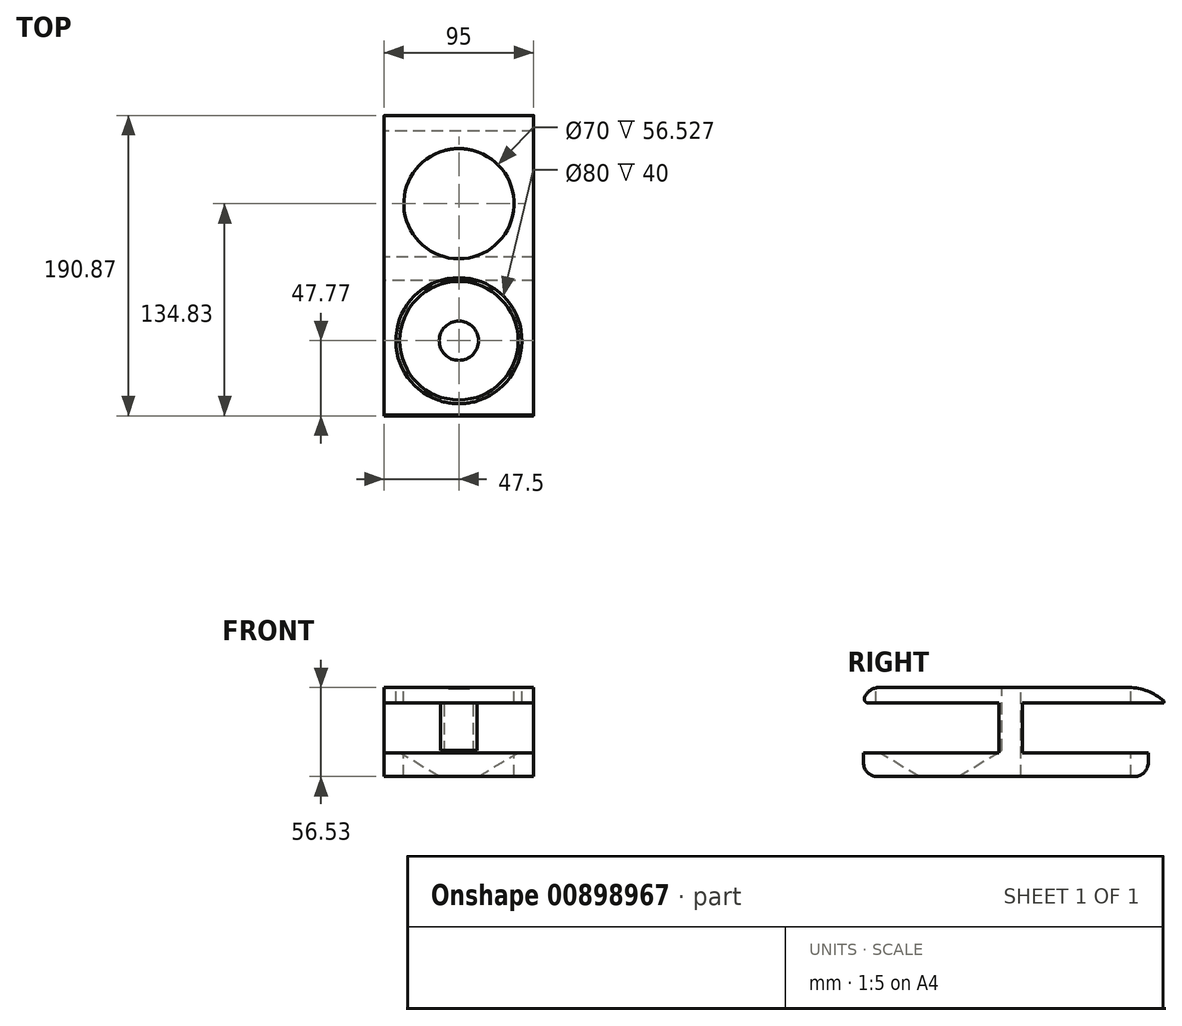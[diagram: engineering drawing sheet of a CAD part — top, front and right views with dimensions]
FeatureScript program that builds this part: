
annotation { "Feature Type Name" : "Feature", "Feature Type Description" : "" }
export const myFeature = defineFeature(function(context is Context, id is Id, definition is map)
    precondition{}
    {
        {
            var Q0;
            Q0=qCreatedBy(makeId("Right.planeOp"),FACE);
            var sketch = newSketch(context, id + "F0", { "sketchPlane" : qUnion([Q0])});
            skLineSegment(sketch, "E0", {"start": v(0, 11.66) * mm, "end": v(90.83, 11.66) * mm});
            skLineSegment(sketch, "E1", {"start": v(90.83, 11.66) * mm, "end": v(90.83, 1.76) * mm});
            skLineSegment(sketch, "E2", {"start": v(90.83, 1.76) * mm, "end": v(0, 1.76) * mm});
            skLineSegment(sketch, "E3", {"start": v(0, 1.76) * mm, "end": v(0, -29.77) * mm});
            skLineSegment(sketch, "E4", {"start": v(0, -29.77) * mm, "end": v(79.76, -29.77) * mm});
            skLineSegment(sketch, "E5", {"start": v(79.76, -29.77) * mm, "end": v(79.76, -44.87) * mm});
            skLineSegment(sketch, "E6", {"start": v(79.76, -44.87) * mm, "end": v(-101.06, -44.87) * mm});
            skLineSegment(sketch, "E7", {"start": v(-101.06, -44.87) * mm, "end": v(-101.06, -29.77) * mm});
            skLineSegment(sketch, "E8", {"start": v(-101.06, -29.77) * mm, "end": v(-15.01, -29.77) * mm});
            skLineSegment(sketch, "E9", {"start": v(-15.01, -29.77) * mm, "end": v(-15.01, 1.76) * mm});
            skLineSegment(sketch, "E10", {"start": v(-15.01, 1.76) * mm, "end": v(-101.06, 1.76) * mm});
            skLineSegment(sketch, "E11", {"start": v(-101.06, 1.76) * mm, "end": v(-101.06, 11.66) * mm});
            skLineSegment(sketch, "E12", {"start": v(-101.06, 11.66) * mm, "end": v(0, 11.66) * mm});
            skSolve(sketch);
        }
        {
            var Q0;
            Q0=makeQuery(id+"F0.imprint","IMPRINT",FACE,{"disambiguationData":[TD([[makeQuery(id+"F0.imprint","IMPRINT",EDGE,{"derivedFrom":sQuery(id+"F0.wireOp",EDGE,"E0")}),-1.0]])]});
            extrude(context, id + "F1", {"entities" : qUnion([Q0]), "depth" : 95 * mm, "offsetDistance" : 25 * mm});
        }
        {
            var Q0;
            Q0=makeQuery(id+"F1.opExtrude","SWEPT_EDGE",EDGE,{"disambiguationData":[OSD([sQuery(id+"F0.wireOp",EDGE,"E11"),sQuery(id+"F0.wireOp",EDGE,"E12")])]});
            fillet(context, id + "F2", {"entities" : qUnion([Q0]), "radius" : 10 * mm, "tangentPropagation" : true, "allowEdgeOverflow" : false});
        }
        {
            var Q0;
            Q0=makeQuery(id+"F1.opExtrude","SWEPT_EDGE",EDGE,{"disambiguationData":[OSD([sQuery(id+"F0.wireOp",EDGE,"E0"),sQuery(id+"F0.wireOp",EDGE,"E1")])]});
            fillet(context, id + "F3", {"entities" : qUnion([Q0]), "radius" : 32.35 * mm, "tangentPropagation" : true, "allowEdgeOverflow" : false});
        }
        {
            var Q0;
            Q0=makeQuery(id+"F1.opExtrude","SWEPT_EDGE",EDGE,{"disambiguationData":[OSD([sQuery(id+"F0.wireOp",EDGE,"E6"),sQuery(id+"F0.wireOp",EDGE,"E7")])]});
            var Q1;
            Q1=makeQuery(id+"F1.opExtrude","SWEPT_EDGE",EDGE,{"disambiguationData":[OSD([sQuery(id+"F0.wireOp",EDGE,"E5"),sQuery(id+"F0.wireOp",EDGE,"E6")])]});
            fillet(context, id + "F4", {"entities" : qUnion([Q0, Q1]), "radius" : 8.74 * mm, "tangentPropagation" : true, "allowEdgeOverflow" : false});
        }
        {
            var Q0;
            Q0=makeQuery(id+"F3.opFillet","BLEND_EDGE",EDGE,{"blendedFrom":[makeQuery(id+"F1.opExtrude","SWEPT_EDGE",EDGE,{"disambiguationData":[OSD([sQuery(id+"F0.wireOp",EDGE,"E0"),sQuery(id+"F0.wireOp",EDGE,"E1")])]}),makeQuery(id+"F1.opExtrude","SWEPT_FACE",FACE,{"disambiguationData":[OSD([sQuery(id+"F0.wireOp",EDGE,"E2")])]})],"blendedInto":[makeQuery(id+"F1.opExtrude","SWEPT_FACE",FACE,{"disambiguationData":[OSD([sQuery(id+"F0.wireOp",EDGE,"E2")])]})]});
            fillet(context, id + "F5", {"entities" : qUnion([Q0]), "radius" : 0.7 * mm, "tangentPropagation" : true, "allowEdgeOverflow" : false});
        }
        {
            var Q0;
            Q0=makeQuery(id+"F2.opFillet","BLEND_EDGE",EDGE,{"blendedFrom":[makeQuery(id+"F1.opExtrude","SWEPT_EDGE",EDGE,{"disambiguationData":[OSD([sQuery(id+"F0.wireOp",EDGE,"E11"),sQuery(id+"F0.wireOp",EDGE,"E12")])]}),makeQuery(id+"F1.opExtrude","SWEPT_FACE",FACE,{"disambiguationData":[OSD([sQuery(id+"F0.wireOp",EDGE,"E10")])]})],"blendedInto":[makeQuery(id+"F1.opExtrude","SWEPT_FACE",FACE,{"disambiguationData":[OSD([sQuery(id+"F0.wireOp",EDGE,"E10")])]})]});
            fillet(context, id + "F6", {"entities" : qUnion([Q0]), "radius" : 2.6 * mm, "tangentPropagation" : true, "allowEdgeOverflow" : false});
        }
        {
            var Q0;
            Q0=makeQuery(id+"F1.opExtrude","SWEPT_FACE",FACE,{"disambiguationData":[OSD([sQuery(id+"F0.wireOp",EDGE,"E0"),sQuery(id+"F0.wireOp",EDGE,"E12")])]});
            var sketch = newSketch(context, id + "F7", { "sketchPlane" : qUnion([Q0])});
            skLineSegment(sketch, "E13", {"start": v(0, 0) * mm, "end": v(95, 67.54) * mm});
            skPoint(sketch, "E14", {"position": v(47.5, 33.77) * mm});
            skLineSegment(sketch, "E15", {"start": v(0, -15.52) * mm, "end": v(95, -91.06) * mm});
            skPoint(sketch, "E16", {"position": v(47.5, -53.3) * mm});
            skSolve(sketch);
        }
        {
            var Q0;
            Q0=sQuery(id+"F7.wireOp",VERTEX,"E14");
            var Q1;
            Q1=makeQuery(id+"F1.opExtrude","SWEPT_BODY",BODY,{"disambiguationData":[OSD([sQuery(id+"F0.wireOp",EDGE,"E0"),sQuery(id+"F0.wireOp",EDGE,"E1"),sQuery(id+"F0.wireOp",EDGE,"E2"),sQuery(id+"F0.wireOp",EDGE,"E3"),sQuery(id+"F0.wireOp",EDGE,"E4"),sQuery(id+"F0.wireOp",EDGE,"E5"),sQuery(id+"F0.wireOp",EDGE,"E6"),sQuery(id+"F0.wireOp",EDGE,"E7"),sQuery(id+"F0.wireOp",EDGE,"E8"),sQuery(id+"F0.wireOp",EDGE,"E9"),sQuery(id+"F0.wireOp",EDGE,"E10"),sQuery(id+"F0.wireOp",EDGE,"E11"),sQuery(id+"F0.wireOp",EDGE,"E12")])]});
            hole(context, id + "F8", {"style" : HoleStyle.SIMPLE, "endStyle" : HoleEndStyle.THROUGH, "holeDiameter" : 70 * mm, "majorDiameter" : 5 * mm, "isTappedThrough" : true, "tappedDepth" : 12 * mm, "tapClearance" : 3, "startFromSketch" : true, "locations" : qUnion([Q0]), "scope" : qUnion([Q1])});
        }
        {
            var Q0;
            Q0=sQuery(id+"F7.wireOp",VERTEX,"E16");
            var Q1;
            Q1=makeQuery(id+"F1.opExtrude","SWEPT_BODY",BODY,{"disambiguationData":[OSD([sQuery(id+"F0.wireOp",EDGE,"E0"),sQuery(id+"F0.wireOp",EDGE,"E1"),sQuery(id+"F0.wireOp",EDGE,"E2"),sQuery(id+"F0.wireOp",EDGE,"E3"),sQuery(id+"F0.wireOp",EDGE,"E4"),sQuery(id+"F0.wireOp",EDGE,"E5"),sQuery(id+"F0.wireOp",EDGE,"E6"),sQuery(id+"F0.wireOp",EDGE,"E7"),sQuery(id+"F0.wireOp",EDGE,"E8"),sQuery(id+"F0.wireOp",EDGE,"E9"),sQuery(id+"F0.wireOp",EDGE,"E10"),sQuery(id+"F0.wireOp",EDGE,"E11"),sQuery(id+"F0.wireOp",EDGE,"E12")])]});
            hole(context, id + "F9", {"style" : HoleStyle.SIMPLE, "endStyle" : HoleEndStyle.BLIND, "holeDiameter" : 80 * mm, "majorDiameter" : 5 * mm, "holeDepth" : 40 * mm, "isTappedThrough" : true, "tappedDepth" : 12 * mm, "tapClearance" : 3, "startFromSketch" : true, "locations" : qUnion([Q0]), "scope" : qUnion([Q1])});
        }
    });
